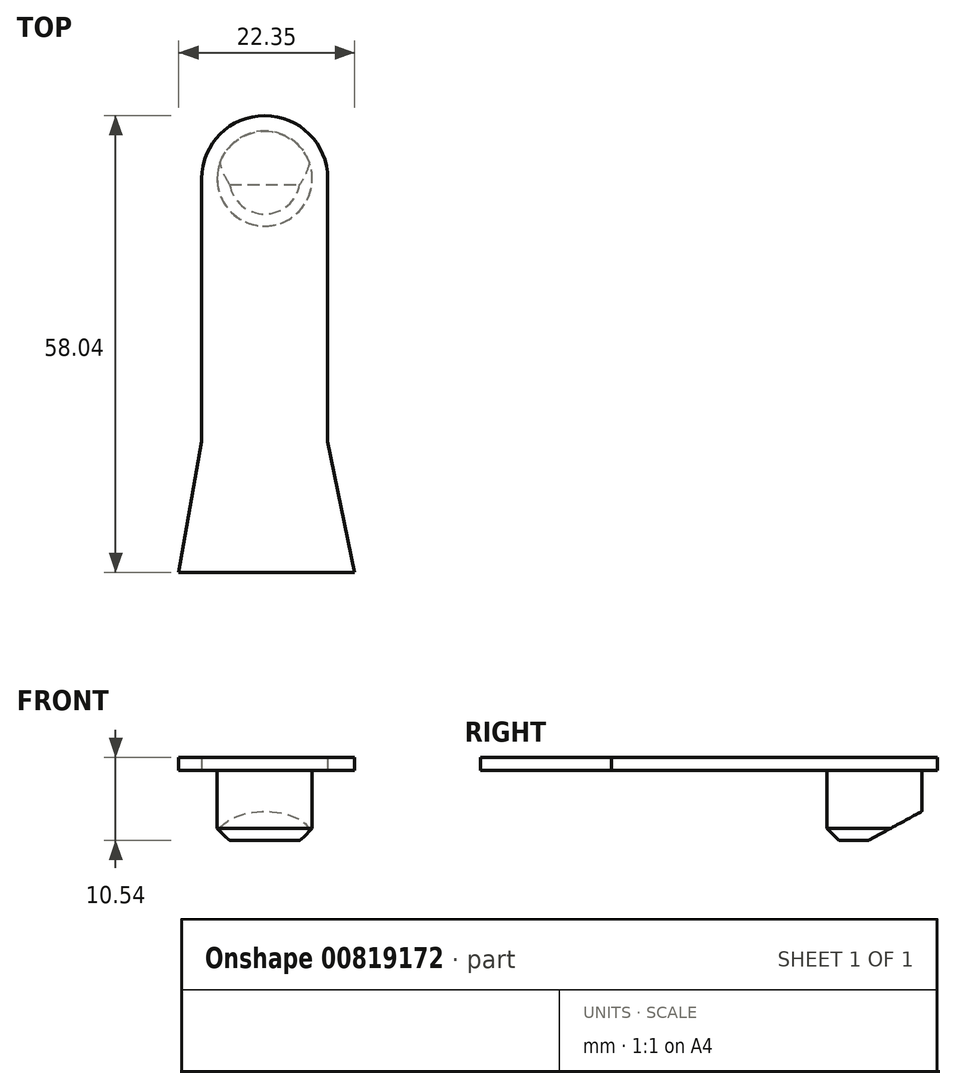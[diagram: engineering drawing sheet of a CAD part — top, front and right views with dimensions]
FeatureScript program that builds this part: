
annotation { "Feature Type Name" : "Feature", "Feature Type Description" : "" }
export const myFeature = defineFeature(function(context is Context, id is Id, definition is map)
    precondition{}
    {
        {
            var Q0;
            Q0=qCreatedBy(makeId("Top.planeOp"),FACE);
            var sketch = newSketch(context, id + "F0", { "sketchPlane" : qUnion([Q0])});
            skLineSegment(sketch, "E0", {"start": v(-8.08, -6.44) * mm, "end": v(-8.08, 26.96) * mm});
            skLineSegment(sketch, "E1", {"start": v(7.92, 26.96) * mm, "end": v(7.92, -6.44) * mm});
            skArc(sketch, "E2", {"start": v(7.92, 26.96) * mm, "mid": v(-0.08, 34.97) * mm, "end": v(-8.08, 26.96) * mm});
            skLineSegment(sketch, "E3", {"start": v(-11.01, -23.07) * mm, "end": v(11.34, -23.07) * mm});
            skLineSegment(sketch, "E4", {"start": v(11.34, -23.07) * mm, "end": v(7.92, -6.44) * mm});
            skLineSegment(sketch, "E5", {"start": v(-8.08, -6.44) * mm, "end": v(-11.01, -23.07) * mm});
            skSolve(sketch);
        }
        {
            var Q0;
            Q0=makeQuery(id+"F0.imprint","IMPRINT",FACE,{"disambiguationData":[TD([[makeQuery(id+"F0.imprint","IMPRINT",EDGE,{"derivedFrom":sQuery(id+"F0.wireOp",EDGE,"E0")}),-1.0]])]});
            extrude(context, id + "F1", {"entities" : qUnion([Q0]), "depth" : 1.65 * mm, "offsetDistance" : 25.4 * mm});
        }
        {
            var Q0;
            Q0=makeQuery(id+"F1.opExtrude","CAP_FACE",FACE,{"disambiguationData":[OSD([sQuery(id+"F0.wireOp",EDGE,"E0"),sQuery(id+"F0.wireOp",EDGE,"E1"),sQuery(id+"F0.wireOp",EDGE,"E2"),sQuery(id+"F0.wireOp",EDGE,"E3"),sQuery(id+"F0.wireOp",EDGE,"E4"),sQuery(id+"F0.wireOp",EDGE,"E5")])],"isStart":true});
            var sketch = newSketch(context, id + "F2", { "sketchPlane" : qUnion([Q0])});
            skCircle(sketch, "E6", {"center": v(-0.08, -26.96) * mm, "radius": 6.03 * mm});
            skSolve(sketch);
        }
        {
            var Q0;
            Q0=makeQuery(id+"F2.imprint","IMPRINT",FACE,{"disambiguationData":[TD([[makeQuery(id+"F2.imprint","IMPRINT",EDGE,{"derivedFrom":sQuery(id+"F2.wireOp",EDGE,"E6")}),1.0]])]});
            extrude(context, id + "F3", {"entities" : qUnion([Q0]), "operationType" : NewBodyOperationType.ADD, "depth" : 8.9 * mm, "offsetDistance" : 25.4 * mm});
        }
        {
            var Q0;
            Q0=makeQuery(id+"F1.opExtrude","SWEPT_FACE",FACE,{"disambiguationData":[OSD([sQuery(id+"F0.wireOp",EDGE,"E0")])]});
            var sketch = newSketch(context, id + "F4", { "sketchPlane" : qUnion([Q0])});
            skLineSegment(sketch, "E7", {"start": v(-34.27, -4.5) * mm, "end": v(-24.26, -9.96) * mm});
            skLineSegment(sketch, "E8", {"start": v(-24.26, -9.96) * mm, "end": v(-34.27, -10.27) * mm});
            skLineSegment(sketch, "E9", {"start": v(-34.27, -4.5) * mm, "end": v(-34.27, -10.27) * mm});
            skSolve(sketch);
        }
        {
            var Q0;
            Q0=makeQuery(id+"F4.imprint","IMPRINT",FACE,{"disambiguationData":[TD([[makeQuery(id+"F4.imprint","IMPRINT",EDGE,{"derivedFrom":sQuery(id+"F4.wireOp",EDGE,"E7")}),-1.0]])]});
            extrude(context, id + "F5", {"entities" : qUnion([Q0]), "operationType" : NewBodyOperationType.REMOVE, "oppositeDirection" : true, "depth" : 17.32 * mm, "offsetDistance" : 25.4 * mm});
        }
        {
            var Q0;
            Q0=makeQuery(id+"F3.opExtrude","CAP_EDGE",EDGE,{"disambiguationData":[OSD([sQuery(id+"F2.wireOp",EDGE,"E6")])],"isStart":false});
            chamfer(context, id + "F6", {"entities" : qUnion([Q0]), "width" : 1.52 * mm, "tangentPropagation" : true});
        }
    });
